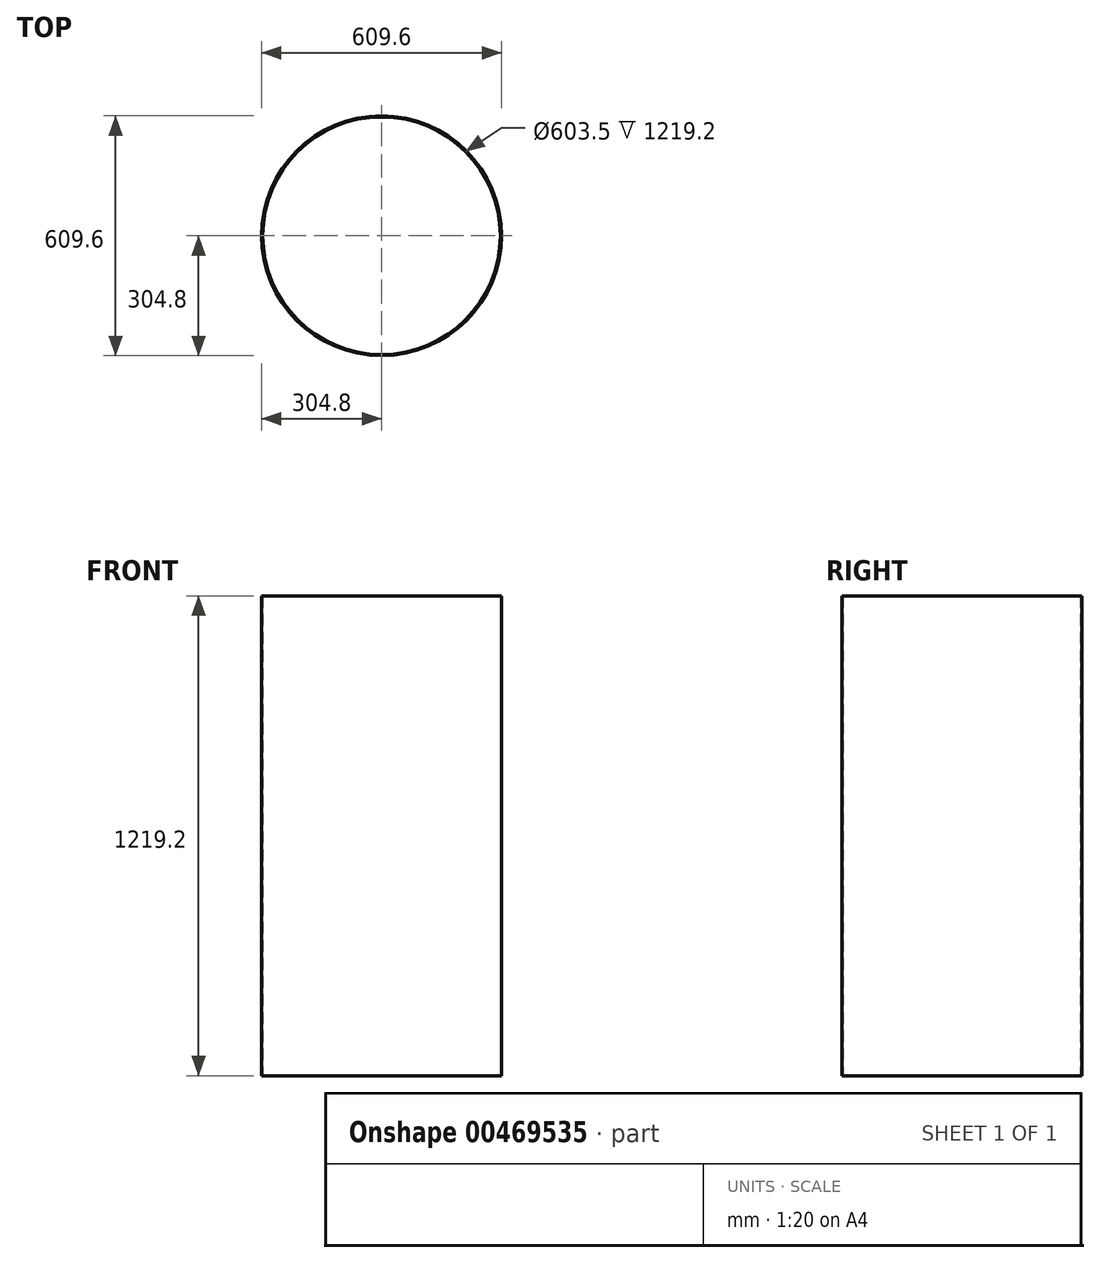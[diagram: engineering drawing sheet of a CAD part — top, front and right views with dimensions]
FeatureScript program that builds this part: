
annotation { "Feature Type Name" : "Feature", "Feature Type Description" : "" }
export const myFeature = defineFeature(function(context is Context, id is Id, definition is map)
    precondition{}
    {
        {
            var Q0;
            Q0=qCreatedBy(makeId("Top.planeOp"),FACE);
            var sketch = newSketch(context, id + "F0", { "sketchPlane" : qUnion([Q0])});
            skCircle(sketch, "E0", {"center": v(0, 0) * mm, "radius": 304.8 * mm});
            skCircle(sketch, "E1", {"center": v(0, 0) * mm, "radius": 301.75 * mm});
            skSolve(sketch);
        }
        {
            var Q0;
            Q0 = qSketchRegion(id + "F0", true);
            extrude(context, id + "F1", {"entities" : qUnion([Q0]), "depth" : 1219.2 * mm, "offsetDistance" : 25.4 * mm});
        }
    });
